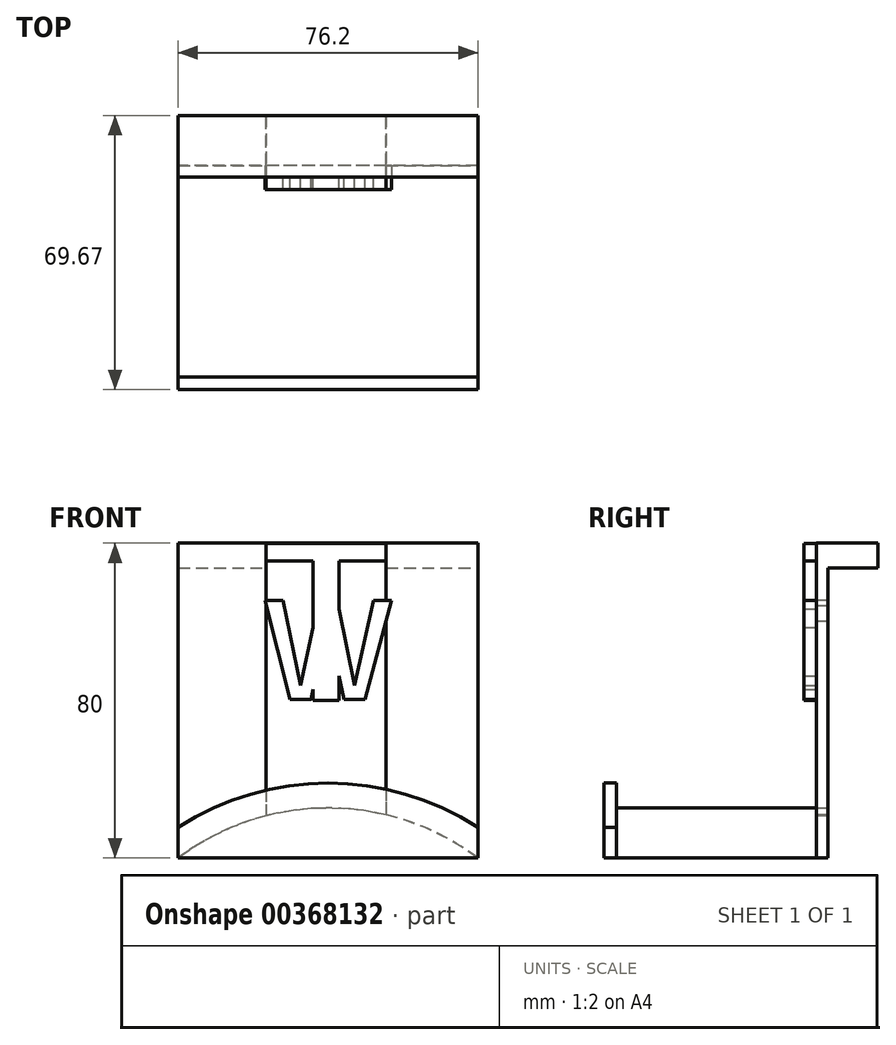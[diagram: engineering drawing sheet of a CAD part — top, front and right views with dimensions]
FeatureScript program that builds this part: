
annotation { "Feature Type Name" : "Feature", "Feature Type Description" : "" }
export const myFeature = defineFeature(function(context is Context, id is Id, definition is map)
    precondition{}
    {
        {
            var Q0;
            Q0=qCreatedBy(makeId("Front.planeOp"),FACE);
            var sketch = newSketch(context, id + "F0", { "sketchPlane" : qUnion([Q0])});
            skLineSegment(sketch, "E0.bottom", {"start": v(38.1, 40) * mm, "end": v(-38.1, 40) * mm});
            skLineSegment(sketch, "E0.top", {"start": v(38.1, -40) * mm, "end": v(-38.1, -40) * mm});
            skLineSegment(sketch, "E0.left", {"start": v(38.1, 40) * mm, "end": v(38.1, -40) * mm});
            skLineSegment(sketch, "E0.right", {"start": v(-38.1, 40) * mm, "end": v(-38.1, -40) * mm});
            skPoint(sketch, "E0.middle", {"position": v(0, 0) * mm});
            skSolve(sketch);
        }
        {
            var Q0;
            Q0 = qSketchRegion(id + "F0", true);
            extrude(context, id + "F1", {"entities" : qUnion([Q0]), "endBound" : BoundingType.SYMMETRIC, "depth" : 3 * mm});
        }
        {
            var Q0;
            Q0=makeQuery(id+"F1.opExtrude","CAP_FACE",FACE,{"disambiguationData":[OSD([sQuery(id+"F0.wireOp",EDGE,"E0.bottom"),sQuery(id+"F0.wireOp",EDGE,"E0.top"),sQuery(id+"F0.wireOp",EDGE,"E0.left"),sQuery(id+"F0.wireOp",EDGE,"E0.right")])],"isStart":true});
            var sketch = newSketch(context, id + "F2", { "sketchPlane" : qUnion([Q0])});
            skLineSegment(sketch, "E1.bottom", {"start": v(38.1, 40) * mm, "end": v(-38.1, 40) * mm});
            skLineSegment(sketch, "E1.top", {"start": v(38.1, 33.65) * mm, "end": v(-38.1, 33.65) * mm});
            skLineSegment(sketch, "E1.left", {"start": v(38.1, 40) * mm, "end": v(38.1, 33.65) * mm});
            skLineSegment(sketch, "E1.right", {"start": v(-38.1, 40) * mm, "end": v(-38.1, 33.65) * mm});
            skSolve(sketch);
        }
        {
            var Q0;
            Q0 = qSketchRegion(id + "F2", true);
            extrude(context, id + "F3", {"entities" : qUnion([Q0]), "operationType" : NewBodyOperationType.ADD, "depth" : 12.7 * mm});
        }
        {
            var Q0;
            Q0=makeQuery(id+"F1.opExtrude","CAP_FACE",FACE,{"disambiguationData":[OSD([sQuery(id+"F0.wireOp",EDGE,"E0.bottom"),sQuery(id+"F0.wireOp",EDGE,"E0.top"),sQuery(id+"F0.wireOp",EDGE,"E0.left"),sQuery(id+"F0.wireOp",EDGE,"E0.right")])],"isStart":false});
            var sketch = newSketch(context, id + "F4", { "sketchPlane" : qUnion([Q0])});
            skArc(sketch, "E2", {"start": v(38.1, -40) * mm, "mid": v(0, -27.3) * mm, "end": v(-38.1, -40) * mm});
            skSolve(sketch);
        }
        {
            var Q0;
            Q0 = qSketchRegion(id + "F4", true);
            var Q1;
            Q1=makeQuery(id+"F4.imprint","IMPRINT",FACE,{"disambiguationData":[TD([[makeQuery(id+"F4.imprint","IMPRINT",EDGE,{"derivedFrom":sQuery(id+"F4.wireOp",EDGE,"E2")}),1.0]])]});
            extrude(context, id + "F5", {"entities" : qUnion([Q0, Q1]), "operationType" : NewBodyOperationType.ADD, "depth" : 50.8 * mm});
        }
        {
            var Q0;
            Q0=makeQuery(id+"F5.opExtrude","CAP_FACE",FACE,{"disambiguationData":[OSD([sQuery(id+"F0.wireOp",EDGE,"E0.top"),sQuery(id+"F4.wireOp",EDGE,"E2")])],"isStart":false});
            var sketch = newSketch(context, id + "F6", { "sketchPlane" : qUnion([Q0])});
            skLineSegment(sketch, "E3.0.0", {"start": v(-38.1, -40) * mm, "end": v(38.1, -40) * mm});
            skArc(sketch, "E3.0.1", {"start": v(38.1, -40) * mm, "mid": v(0, -27.3) * mm, "end": v(-38.1, -40) * mm});
            skArc(sketch, "E4", {"start": v(38.1, -32.26) * mm, "mid": v(0, -20.95) * mm, "end": v(-38.1, -32.26) * mm});
            skLineSegment(sketch, "E5", {"start": v(-38.1, -40) * mm, "end": v(-38.1, -32.26) * mm});
            skLineSegment(sketch, "E6", {"start": v(38.1, -40) * mm, "end": v(38.1, -32.26) * mm});
            skSolve(sketch);
        }
        {
            var Q0;
            Q0 = qSketchRegion(id + "F6", true);
            extrude(context, id + "F7", {"entities" : qUnion([Q0]), "operationType" : NewBodyOperationType.ADD, "depth" : 3.17 * mm});
        }
        {
            var Q0;
            Q0=makeQuery(id+"F1.opExtrude","CAP_FACE",FACE,{"disambiguationData":[OSD([sQuery(id+"F0.wireOp",EDGE,"E0.bottom"),sQuery(id+"F0.wireOp",EDGE,"E0.top"),sQuery(id+"F0.wireOp",EDGE,"E0.left"),sQuery(id+"F0.wireOp",EDGE,"E0.right")])],"isStart":false});
            var sketch = newSketch(context, id + "F8", { "sketchPlane" : qUnion([Q0])});
            skText(sketch, "E7", { "text": "T", "fontName": "AllertaStencil-Regular.ttf"});
            skText(sketch, "E8", { "text": "W", "fontName": "AllertaStencil-Regular.ttf"});
            skLineSegment(sketch, "E9", {"start": v(-18.46, 40) * mm, "end": v(-18.46, -30.04) * mm});
            skLineSegment(sketch, "E10", {"start": v(18.46, 40) * mm, "end": v(18.46, -30.04) * mm});
            const initialGuessF8  = {"E7": [-0.01846, 0, 1, 0, 0.04], "E8": [-0.01846, 0.00046, 1, 0, 0.02496]};
            skSetInitialGuess(sketch, initialGuessF8);
            skSolve(sketch);
        }
        {
            var Q0;
            Q0 = qSketchRegion(id + "F8", true);
            extrude(context, id + "F9", {"entities" : qUnion([Q0]), "operationType" : NewBodyOperationType.ADD, "depth" : 3.17 * mm});
        }
        {
            var Q0;
            Q0=makeQuery(id+"F1.opExtrude","CAP_FACE",FACE,{"disambiguationData":[OSD([sQuery(id+"F0.wireOp",EDGE,"E0.bottom"),sQuery(id+"F0.wireOp",EDGE,"E0.top"),sQuery(id+"F0.wireOp",EDGE,"E0.left"),sQuery(id+"F0.wireOp",EDGE,"E0.right")])],"isStart":false});
            var sketch = newSketch(context, id + "F10", { "sketchPlane" : qUnion([Q0])});
            skLineSegment(sketch, "E11", {"start": v(-15.7, 39.98) * mm, "end": v(-15.7, -29.27) * mm});
            skLineSegment(sketch, "E12", {"start": v(14.74, 39.98) * mm, "end": v(14.74, -29.04) * mm});
            skLineSegment(sketch, "E13.0.0", {"start": v(6.76, 3.88) * mm, "end": v(2.8, 23.22) * mm});
            skLineSegment(sketch, "E13.0.1", {"start": v(2.8, 23.22) * mm, "end": v(2.8, 35.54) * mm});
            skLineSegment(sketch, "E13.0.2", {"start": v(2.8, 35.54) * mm, "end": v(14.74, 35.54) * mm});
            skLineSegment(sketch, "E13.0.3", {"start": v(14.74, 35.54) * mm, "end": v(14.74, 39.98) * mm});
            skLineSegment(sketch, "E13.0.4", {"start": v(14.74, 39.98) * mm, "end": v(-15.7, 39.98) * mm});
            skLineSegment(sketch, "E13.0.5", {"start": v(-15.7, 39.98) * mm, "end": v(-15.7, 35.54) * mm});
            skLineSegment(sketch, "E13.0.6", {"start": v(-15.7, 35.54) * mm, "end": v(-3.75, 35.54) * mm});
            skLineSegment(sketch, "E13.0.7", {"start": v(-3.75, 35.54) * mm, "end": v(-3.75, 18.54) * mm});
            skLineSegment(sketch, "E13.0.8", {"start": v(-3.75, 18.54) * mm, "end": v(-6.98, 3.88) * mm});
            skLineSegment(sketch, "E13.0.9", {"start": v(-6.98, 3.88) * mm, "end": v(-11.39, 25.4) * mm});
            skLineSegment(sketch, "E13.0.10", {"start": v(-11.39, 25.4) * mm, "end": v(-15.99, 25.4) * mm});
            skLineSegment(sketch, "E13.0.11", {"start": v(-15.99, 25.4) * mm, "end": v(-9.66, 0.32) * mm});
            skLineSegment(sketch, "E13.0.12", {"start": v(-9.66, 0.32) * mm, "end": v(-4.34, 0.32) * mm});
            skLineSegment(sketch, "E13.0.13", {"start": v(-4.34, 0.32) * mm, "end": v(-3.75, 2.88) * mm});
            skLineSegment(sketch, "E13.0.14", {"start": v(-3.75, 2.88) * mm, "end": v(-3.75, 0) * mm});
            skLineSegment(sketch, "E13.0.15", {"start": v(-3.75, 0) * mm, "end": v(2.8, 0) * mm});
            skLineSegment(sketch, "E13.0.16", {"start": v(2.8, 0) * mm, "end": v(2.8, 6.3) * mm});
            skLineSegment(sketch, "E13.0.17", {"start": v(2.8, 6.3) * mm, "end": v(4.12, 0.32) * mm});
            skLineSegment(sketch, "E13.0.18", {"start": v(4.12, 0.32) * mm, "end": v(9.4, 0.32) * mm});
            skLineSegment(sketch, "E13.0.19", {"start": v(9.4, 0.32) * mm, "end": v(16.14, 25.4) * mm});
            skLineSegment(sketch, "E13.0.20", {"start": v(16.14, 25.4) * mm, "end": v(11.54, 25.4) * mm});
            skLineSegment(sketch, "E13.0.21", {"start": v(11.54, 25.4) * mm, "end": v(6.76, 3.88) * mm});
            skArc(sketch, "E14.0", {"start": v(38.1, -40) * mm, "mid": v(0, -27.3) * mm, "end": v(-38.1, -40) * mm});
            skSolve(sketch);
        }
        {
            var Q0;
            Q0 = qSketchRegion(id + "F10", true);
            extrude(context, id + "F11", {"entities" : qUnion([Q0]), "operationType" : NewBodyOperationType.REMOVE, "endBound" : BoundingType.THROUGH_ALL, "oppositeDirection" : true, "depth" : 25.4 * mm});
        }
    });
